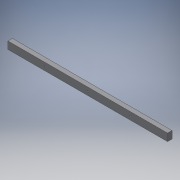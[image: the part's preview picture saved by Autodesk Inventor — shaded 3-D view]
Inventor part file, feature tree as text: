
AUTODESK INVENTOR PART (.ipt)
format: ipt  version: 2019 (Build 230136000, 136)  size: 113,664 bytes
history: native  units: in
note: dims shown in document units (in); Inventor stores cm internally (conversion verified against a paired STEP export)
features: extrude x2, sketch x2, other x2, reference x1, helix x1
ambient origin geometry x8: Origin, YZ Plane, XZ Plane, XY Plane, X Axis, Y Axis, Z Axis, Center Point
bodies: Solid1 (feature_tree)
feature tree (8):
  extrude  "Extrusion1"  Depth=0.4724in TaperAngle=0.0deg
  extrude  "Extrusion2"  Depth=16.9291in
  sketch  "Sketch1"  dims[d1=0.7874in d2=0.4724in d3=0.0in]
  reference  "Reference1"
  sketch  "Sketch2"  dims[d4=0.1654in d5=3.937in d6=0.1654in d7=3.937in d8=0.1654in d9=0.3937in d10=0.0in d11=16.9291in]
  other  "<userpath>\Documents\CAD Files\Helix DLP\Helix DLP.iam"
  helix  "Helix DLP.iam"  [1 undecoded]
  other  "Tank2:1"
note: 1 required parameter value undecoded (feature->parameter linkage not recoverable at this tier; creation-order binding heuristic only, values carry confidence <= 0.55)
